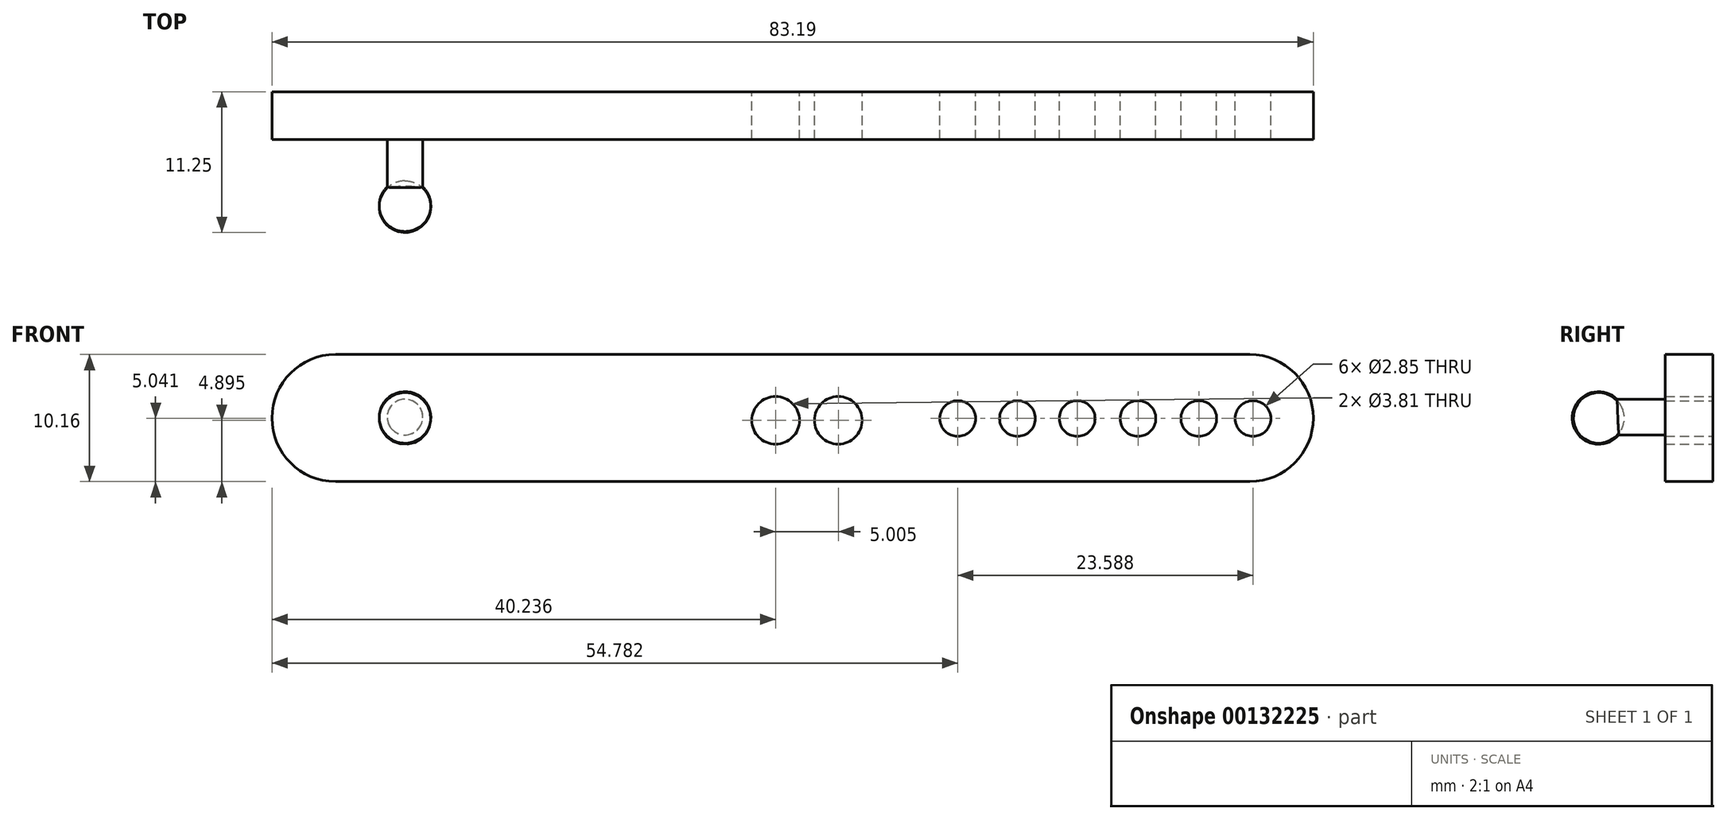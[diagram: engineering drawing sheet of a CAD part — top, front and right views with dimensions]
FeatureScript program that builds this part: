
annotation { "Feature Type Name" : "Feature", "Feature Type Description" : "" }
export const myFeature = defineFeature(function(context is Context, id is Id, definition is map)
    precondition{}
    {
        {
            var Q0;
            Q0=qCreatedBy(makeId("Front.planeOp"),FACE);
            var sketch = newSketch(context, id + "F0", { "sketchPlane" : qUnion([Q0])});
            skLineSegment(sketch, "E0.bottom", {"start": v(-37.66, 36.05) * mm, "end": v(35.37, 36.05) * mm});
            skLineSegment(sketch, "E0.top", {"start": v(-37.66, 25.9) * mm, "end": v(35.37, 25.9) * mm});
            skLineSegment(sketch, "E0.left", {"start": v(-37.66, 36.05) * mm, "end": v(-37.66, 25.9) * mm});
            skLineSegment(sketch, "E0.right", {"start": v(35.37, 36.05) * mm, "end": v(35.37, 25.9) * mm});
            skArc(sketch, "E1", {"start": v(35.37, 25.9) * mm, "mid": v(40.45, 30.97) * mm, "end": v(35.37, 36.05) * mm});
            skArc(sketch, "E2", {"start": v(-37.66, 36.05) * mm, "mid": v(-42.74, 30.97) * mm, "end": v(-37.66, 25.9) * mm});
            skSolve(sketch);
        }
        {
            var Q0;
            Q0=makeQuery(id+"F0.imprint","IMPRINT",FACE,{"disambiguationData":[TD([[makeQuery(id+"F0.imprint","IMPRINT",EDGE,{"derivedFrom":sQuery(id+"F0.wireOp",EDGE,"E0.bottom")}),-1.0]])]});
            var Q1;
            Q1=makeQuery(id+"F0.imprint","IMPRINT",FACE,{"disambiguationData":[TD([[makeQuery(id+"F0.imprint","IMPRINT",EDGE,{"derivedFrom":sQuery(id+"F0.wireOp",EDGE,"E0.left")}),-1.0]])]});
            var Q2;
            Q2=makeQuery(id+"F0.imprint","IMPRINT",FACE,{"disambiguationData":[TD([[makeQuery(id+"F0.imprint","IMPRINT",EDGE,{"derivedFrom":sQuery(id+"F0.wireOp",EDGE,"E0.right")}),1.0]])]});
            extrude(context, id + "F1", {"entities" : qUnion([Q0, Q1, Q2]), "depth" : 3.8 * mm});
        }
        {
            var Q0;
            Q0=makeQuery(id+"F1.opExtrude","CAP_FACE",FACE,{"disambiguationData":[OSD([sQuery(id+"F0.wireOp",EDGE,"E0.bottom"),sQuery(id+"F0.wireOp",EDGE,"E0.top"),sQuery(id+"F0.wireOp",EDGE,"E1"),sQuery(id+"F0.wireOp",EDGE,"E2")])],"isStart":true});
            var sketch = newSketch(context, id + "F2", { "sketchPlane" : qUnion([Q0])});
            skCircle(sketch, "E3", {"center": v(2.5, 30.79) * mm, "radius": 1.9 * mm});
            skCircle(sketch, "E4", {"center": v(-2.5, 30.79) * mm, "radius": 1.9 * mm});
            skSolve(sketch);
        }
        {
            var Q0;
            Q0=makeQuery(id+"F2.imprint","IMPRINT",FACE,{"disambiguationData":[TD([[makeQuery(id+"F2.imprint","IMPRINT",EDGE,{"derivedFrom":sQuery(id+"F2.wireOp",EDGE,"E4")}),1.0]])]});
            var Q1;
            Q1=makeQuery(id+"F2.imprint","IMPRINT",FACE,{"disambiguationData":[TD([[makeQuery(id+"F2.imprint","IMPRINT",EDGE,{"derivedFrom":sQuery(id+"F2.wireOp",EDGE,"E3")}),1.0]])]});
            extrude(context, id + "F3", {"entities" : qUnion([Q0, Q1]), "operationType" : NewBodyOperationType.REMOVE, "oppositeDirection" : true, "depth" : 25.4 * mm});
        }
        {
            var Q0;
            Q0=makeQuery(id+"F1.opExtrude","CAP_FACE",FACE,{"disambiguationData":[OSD([sQuery(id+"F0.wireOp",EDGE,"E0.bottom"),sQuery(id+"F0.wireOp",EDGE,"E0.top"),sQuery(id+"F0.wireOp",EDGE,"E1"),sQuery(id+"F0.wireOp",EDGE,"E2")])],"isStart":false});
            var sketch = newSketch(context, id + "F4", { "sketchPlane" : qUnion([Q0])});
            skCircle(sketch, "E5", {"center": v(-32.1, 31.05) * mm, "radius": 1.43 * mm});
            skCircle(sketch, "E6", {"center": v(-27.5, 31.05) * mm, "radius": 1.43 * mm});
            skCircle(sketch, "E7", {"center": v(-22.56, 31.05) * mm, "radius": 1.43 * mm});
            skCircle(sketch, "E8", {"center": v(-17.7, 31.05) * mm, "radius": 1.43 * mm});
            skCircle(sketch, "E9", {"center": v(-12.85, 31.05) * mm, "radius": 1.43 * mm});
            skCircle(sketch, "E10", {"center": v(12.04, 30.93) * mm, "radius": 1.43 * mm});
            skCircle(sketch, "E11", {"center": v(16.82, 30.93) * mm, "radius": 1.43 * mm});
            skCircle(sketch, "E12", {"center": v(21.59, 30.93) * mm, "radius": 1.43 * mm});
            skCircle(sketch, "E13", {"center": v(26.44, 30.93) * mm, "radius": 1.43 * mm});
            skCircle(sketch, "E14", {"center": v(31.3, 30.93) * mm, "radius": 1.43 * mm});
            skCircle(sketch, "E15", {"center": v(35.63, 30.93) * mm, "radius": 1.43 * mm});
            skSolve(sketch);
        }
        {
            var Q0;
            Q0=makeQuery(id+"F4.imprint","IMPRINT",FACE,{"disambiguationData":[TD([[makeQuery(id+"F4.imprint","IMPRINT",EDGE,{"derivedFrom":sQuery(id+"F4.wireOp",EDGE,"E5")}),1.0]])]});
            var Q1;
            Q1=sQuery(id+"F4.wireOp",EDGE,"E5");
            extrude(context, id + "F5", {"entities" : qUnion([Q0]), "surfaceEntities" : qUnion([Q1]), "depth" : 5.33 * mm});
        }
        {
            var Q0;
            Q0=makeQuery(id+"F5.opExtrude","CAP_FACE",FACE,{"disambiguationData":[OSD([sQuery(id+"F4.wireOp",EDGE,"E5")])],"isStart":false});
            var sketch = newSketch(context, id + "F6", { "sketchPlane" : qUnion([Q0])});
            skLineSegment(sketch, "E16", {"start": v(-34.17, 30.98) * mm, "end": v(-30.04, 30.98) * mm});
            skArc(sketch, "E17", {"start": v(-30.04, 30.98) * mm, "mid": v(-32.1, 33.09) * mm, "end": v(-34.17, 30.98) * mm});
            skSolve(sketch);
        }
        {
            var Q0;
            {var subQ0=sQuery(id+"F6.wireOp",EDGE,"E17");Q0=makeQuery(id+"F6.imprint","IMPRINT",FACE,{"disambiguationData":[TD([[makeQuery(id+"F6.imprint","IMPRINT",EDGE,{"derivedFrom":subQ0}),1.0]])]});}
            var Q1;
            {var subQ0=sQuery(id+"F6.wireOp",EDGE,"E16");var subQ1=makeQuery(id+"F5.opExtrude","CAP_EDGE",EDGE,{"disambiguationData":[OSD([sQuery(id+"F4.wireOp",EDGE,"E5")])],"isStart":false});var subQ2=makeQuery(id+"F6.imprint","INTERSECT",VERTEX,{"disambiguationData":[OD(0.0)],"derivedFrom":[subQ1,subQ0]});Q1=makeQuery(id+"F6.imprint","IMPRINT",FACE,{"disambiguationData":[TD([[makeQuery(id+"F6.imprint","IMPRINT",EDGE,{"disambiguationData":[TD([[subQ2,-1.0]])],"derivedFrom":subQ0}),1.0]])]});}
            var Q2;
            Q2=sQuery(id+"F6.wireOp",EDGE,"E16");
            revolve(context, id + "F7", {"operationType" : NewBodyOperationType.ADD, "entities" : qUnion([Q0, Q1]), "axis" : qUnion([Q2]), "revolveType" : RevolveType.FULL});
        }
        {
            var Q0;
            Q0=makeQuery(id+"F4.imprint","IMPRINT",FACE,{"disambiguationData":[TD([[makeQuery(id+"F4.imprint","IMPRINT",EDGE,{"derivedFrom":sQuery(id+"F4.wireOp",EDGE,"E10")}),1.0]])]});
            var Q1;
            Q1=makeQuery(id+"F4.imprint","IMPRINT",FACE,{"disambiguationData":[TD([[makeQuery(id+"F4.imprint","IMPRINT",EDGE,{"derivedFrom":sQuery(id+"F4.wireOp",EDGE,"E11")}),1.0]])]});
            var Q2;
            Q2=makeQuery(id+"F4.imprint","IMPRINT",FACE,{"disambiguationData":[TD([[makeQuery(id+"F4.imprint","IMPRINT",EDGE,{"derivedFrom":sQuery(id+"F4.wireOp",EDGE,"E12")}),1.0]])]});
            var Q3;
            Q3=makeQuery(id+"F4.imprint","IMPRINT",FACE,{"disambiguationData":[TD([[makeQuery(id+"F4.imprint","IMPRINT",EDGE,{"derivedFrom":sQuery(id+"F4.wireOp",EDGE,"E14")}),1.0]])]});
            var Q4;
            Q4=makeQuery(id+"F4.imprint","IMPRINT",FACE,{"disambiguationData":[TD([[makeQuery(id+"F4.imprint","IMPRINT",EDGE,{"derivedFrom":sQuery(id+"F4.wireOp",EDGE,"E13")}),1.0]])]});
            var Q5;
            Q5=makeQuery(id+"F4.imprint","IMPRINT",FACE,{"disambiguationData":[TD([[makeQuery(id+"F4.imprint","IMPRINT",EDGE,{"derivedFrom":sQuery(id+"F4.wireOp",EDGE,"E15")}),1.0]])]});
            var Q6;
            Q6=sQuery(id+"F4.wireOp",EDGE,"E10");
            var Q7;
            Q7=sQuery(id+"F4.wireOp",EDGE,"E11");
            var Q8;
            Q8=sQuery(id+"F4.wireOp",EDGE,"E12");
            var Q9;
            Q9=sQuery(id+"F4.wireOp",EDGE,"E13");
            var Q10;
            Q10=sQuery(id+"F4.wireOp",EDGE,"E14");
            var Q11;
            Q11=sQuery(id+"F4.wireOp",EDGE,"E15");
            extrude(context, id + "F8", {"entities" : qUnion([Q0, Q1, Q2, Q3, Q4, Q5]), "operationType" : NewBodyOperationType.REMOVE, "surfaceEntities" : qUnion([Q6, Q7, Q8, Q9, Q10, Q11]), "endBound" : BoundingType.SYMMETRIC, "depth" : 25.4 * mm});
        }
    });
